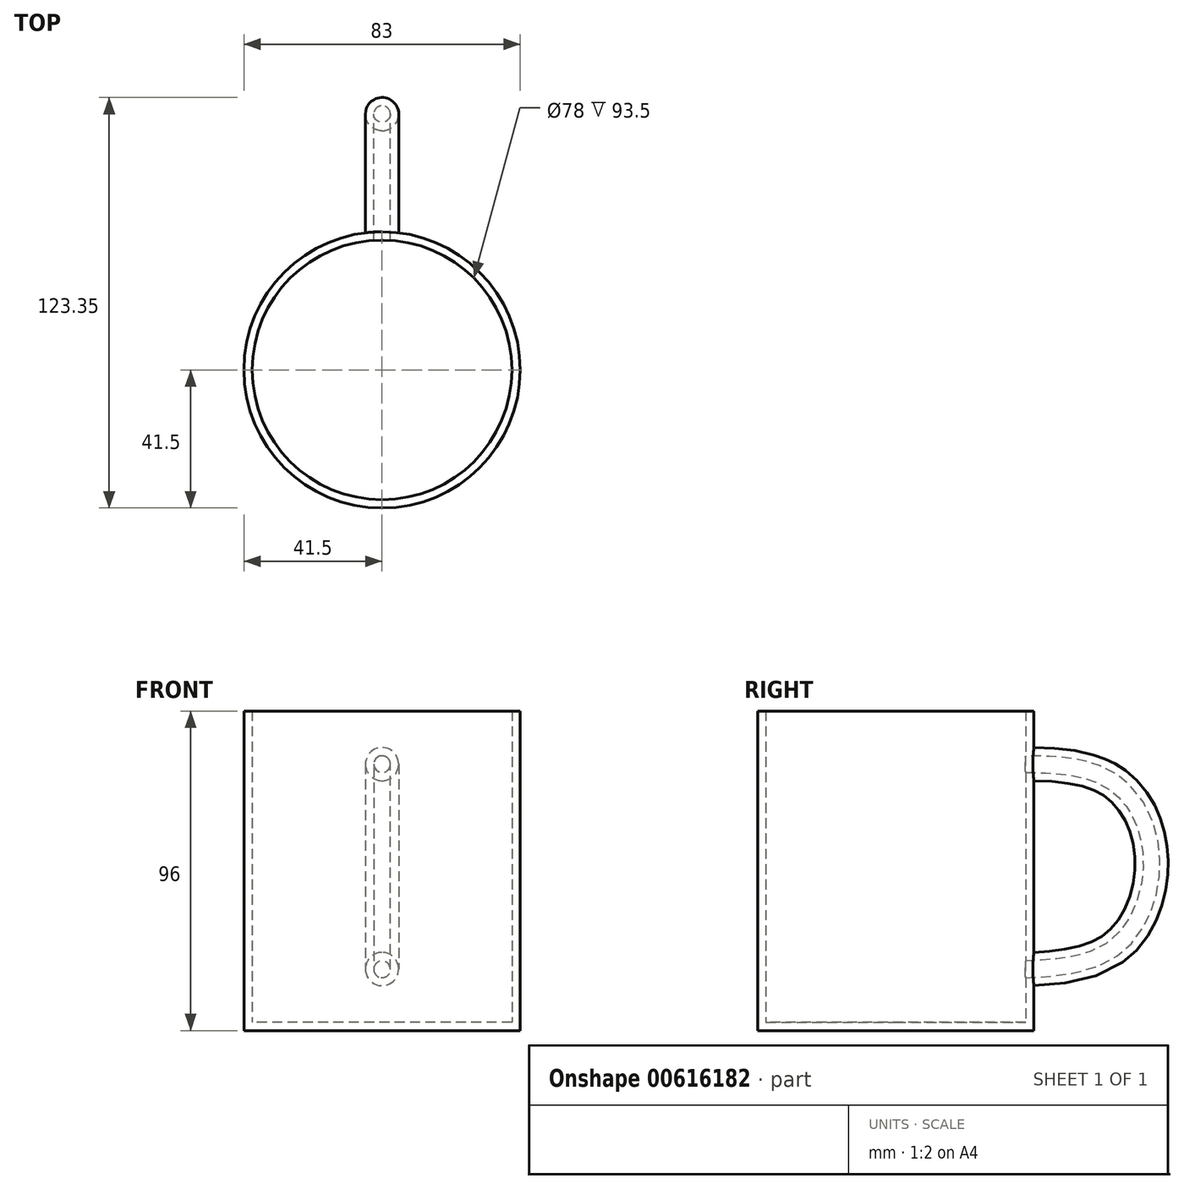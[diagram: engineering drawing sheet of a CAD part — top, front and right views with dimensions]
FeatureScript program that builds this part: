
annotation { "Feature Type Name" : "Feature", "Feature Type Description" : "" }
export const myFeature = defineFeature(function(context is Context, id is Id, definition is map)
    precondition{}
    {
        {
            var Q0;
            Q0=qCreatedBy(makeId("Top.planeOp"),FACE);
            var sketch = newSketch(context, id + "F0", { "sketchPlane" : qUnion([Q0])});
            skCircle(sketch, "E0", {"center": v(0, 0) * mm, "radius": 41.5 * mm});
            skSolve(sketch);
        }
        {
            var Q0;
            Q0 = qSketchRegion(id + "F0", true);
            extrude(context, id + "F1", {"entities" : qUnion([Q0]), "depth" : 96 * mm, "offsetDistance" : 25 * mm});
        }
        {
            var Q0;
            Q0=qCreatedBy(makeId("Right.planeOp"),FACE);
            var sketch = newSketch(context, id + "F2", { "sketchPlane" : qUnion([Q0])});
            skFitSpline(sketch, "E1", {"points": [v(23.95, 81.56) * mm, v(66.62, 76.34) * mm, v(78.95, 50.74) * mm, v(65.67, 22.29) * mm, v(33.43, 16.12) * mm], "startDerivative": vector(194.7, 11.8) * mm, "endDerivative": vector(-116.01, -3.72) * mm});
            skSolve(sketch);
        }
        {
            var Q0;
            Q0=qCreatedBy(makeId("Front.planeOp"),FACE);
            cPlane(context, id + "F3", {"entities" : qUnion([Q0]), "cplaneType" : CPlaneType.OFFSET, "offset" : 40 * mm, "oppositeDirection" : true, "width" : 150 * mm, "height" : 150 * mm});
        }
        {
            var Q0;
            Q0=qCreatedBy(id+"F3.planeOp",FACE);
            var sketch = newSketch(context, id + "F4", { "sketchPlane" : qUnion([Q0])});
            skCircle(sketch, "E2", {"center": v(0, 80.06) * mm, "radius": 5 * mm});
            skSolve(sketch);
        }
        {
            var Q0;
            Q0 = qSketchRegion(id + "F4", true);
            var Q1;
            Q1=sQuery(id+"F2.wireOp",EDGE,"E1");
            sweep(context, id + "F5", {"operationType" : NewBodyOperationType.ADD, "profiles" : qUnion([Q0]), "path" : qUnion([Q1])});
        }
        {
            var Q0;
            Q0=makeQuery(id+"F1.opExtrude","CAP_FACE",FACE,{"disambiguationData":[OSD([sQuery(id+"F0.wireOp",EDGE,"E0")])],"isStart":false});
            shell(context, id + "F6", {"entities" : qUnion([Q0]), "thickness" : 2.5 * mm});
        }
    });
